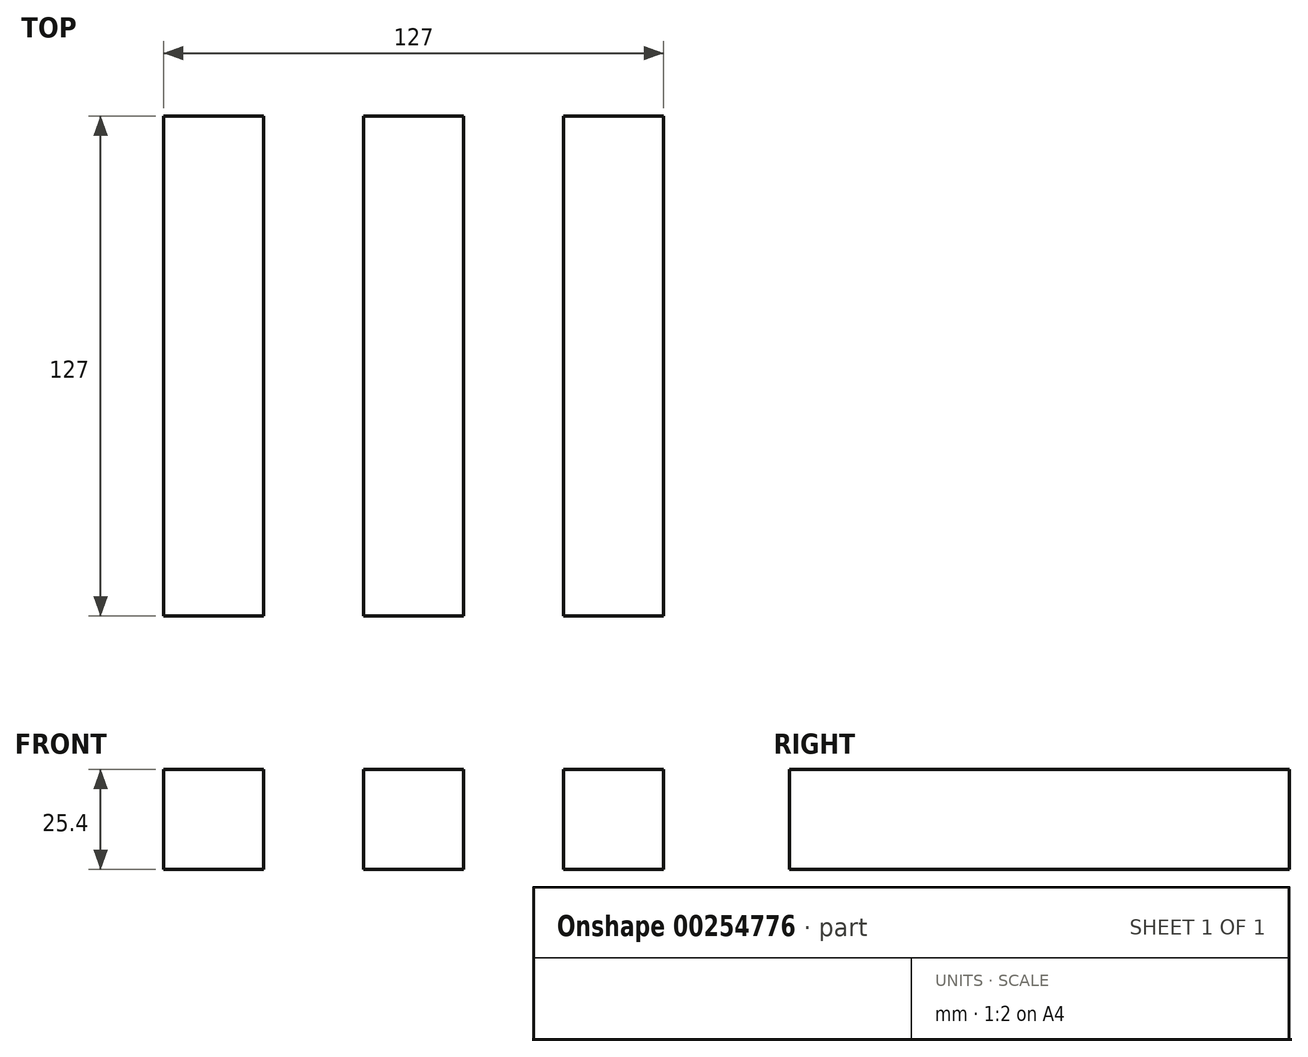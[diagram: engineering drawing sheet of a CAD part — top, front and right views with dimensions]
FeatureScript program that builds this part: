
annotation { "Feature Type Name" : "Feature", "Feature Type Description" : "" }
export const myFeature = defineFeature(function(context is Context, id is Id, definition is map)
    precondition{}
    {
        {
            var Q0;
            Q0=qCreatedBy(makeId("Front.planeOp"),FACE);
            var sketch = newSketch(context, id + "F0", { "sketchPlane" : qUnion([Q0])});
            skLineSegment(sketch, "E0", {"start": v(-50.8, 0) * mm, "end": v(0, 0) * mm});
            skLineSegment(sketch, "E1", {"start": v(0, 0) * mm, "end": v(50.8, 0) * mm});
            skLineSegment(sketch, "E2.bottom", {"start": v(-12.7, -12.7) * mm, "end": v(12.7, -12.7) * mm});
            skLineSegment(sketch, "E2.top", {"start": v(-12.7, 12.7) * mm, "end": v(12.7, 12.7) * mm});
            skLineSegment(sketch, "E2.left", {"start": v(-12.7, -12.7) * mm, "end": v(-12.7, 12.7) * mm});
            skLineSegment(sketch, "E2.right", {"start": v(12.7, -12.7) * mm, "end": v(12.7, 12.7) * mm});
            skPoint(sketch, "E2.middle", {"position": v(0, 0) * mm});
            skLineSegment(sketch, "E3.bottom", {"start": v(-63.5, -12.7) * mm, "end": v(-38.1, -12.7) * mm});
            skLineSegment(sketch, "E3.top", {"start": v(-63.5, 12.7) * mm, "end": v(-38.1, 12.7) * mm});
            skLineSegment(sketch, "E3.left", {"start": v(-63.5, -12.7) * mm, "end": v(-63.5, 12.7) * mm});
            skLineSegment(sketch, "E3.right", {"start": v(-38.1, -12.7) * mm, "end": v(-38.1, 12.7) * mm});
            skPoint(sketch, "E3.middle", {"position": v(-50.8, 0) * mm});
            skLineSegment(sketch, "E4.bottom", {"start": v(63.5, -12.7) * mm, "end": v(38.1, -12.7) * mm});
            skLineSegment(sketch, "E4.top", {"start": v(63.5, 12.7) * mm, "end": v(38.1, 12.7) * mm});
            skLineSegment(sketch, "E4.left", {"start": v(63.5, -12.7) * mm, "end": v(63.5, 12.7) * mm});
            skLineSegment(sketch, "E4.right", {"start": v(38.1, -12.7) * mm, "end": v(38.1, 12.7) * mm});
            skPoint(sketch, "E4.middle", {"position": v(50.8, 0) * mm});
            skSolve(sketch);
        }
        {
            var Q0;
            {var subQ1=sQuery(id+"F0.wireOp",EDGE,"E4.bottom");Q0=makeQuery(id+"F0.imprint","IMPRINT",FACE,{"disambiguationData":[TD([[makeQuery(id+"F0.imprint","IMPRINT",EDGE,{"derivedFrom":subQ1}),-1.0]])]});}
            var Q1;
            {var subQ1=sQuery(id+"F0.wireOp",EDGE,"E3.bottom");Q1=makeQuery(id+"F0.imprint","IMPRINT",FACE,{"disambiguationData":[TD([[makeQuery(id+"F0.imprint","IMPRINT",EDGE,{"derivedFrom":subQ1}),1.0]])]});}
            var Q2;
            {var subQ1=sQuery(id+"F0.wireOp",EDGE,"E2.top");Q2=makeQuery(id+"F0.imprint","IMPRINT",FACE,{"disambiguationData":[TD([[makeQuery(id+"F0.imprint","IMPRINT",EDGE,{"derivedFrom":subQ1}),-1.0]])]});}
            var Q3;
            {var subQ1=sQuery(id+"F0.wireOp",EDGE,"E2.bottom");Q3=makeQuery(id+"F0.imprint","IMPRINT",FACE,{"disambiguationData":[TD([[makeQuery(id+"F0.imprint","IMPRINT",EDGE,{"derivedFrom":subQ1}),1.0]])]});}
            extrude(context, id + "F1", {"entities" : qUnion([Q0, Q1, Q2, Q3]), "endBound" : BoundingType.SYMMETRIC, "depth" : 127 * mm});
        }
    });
